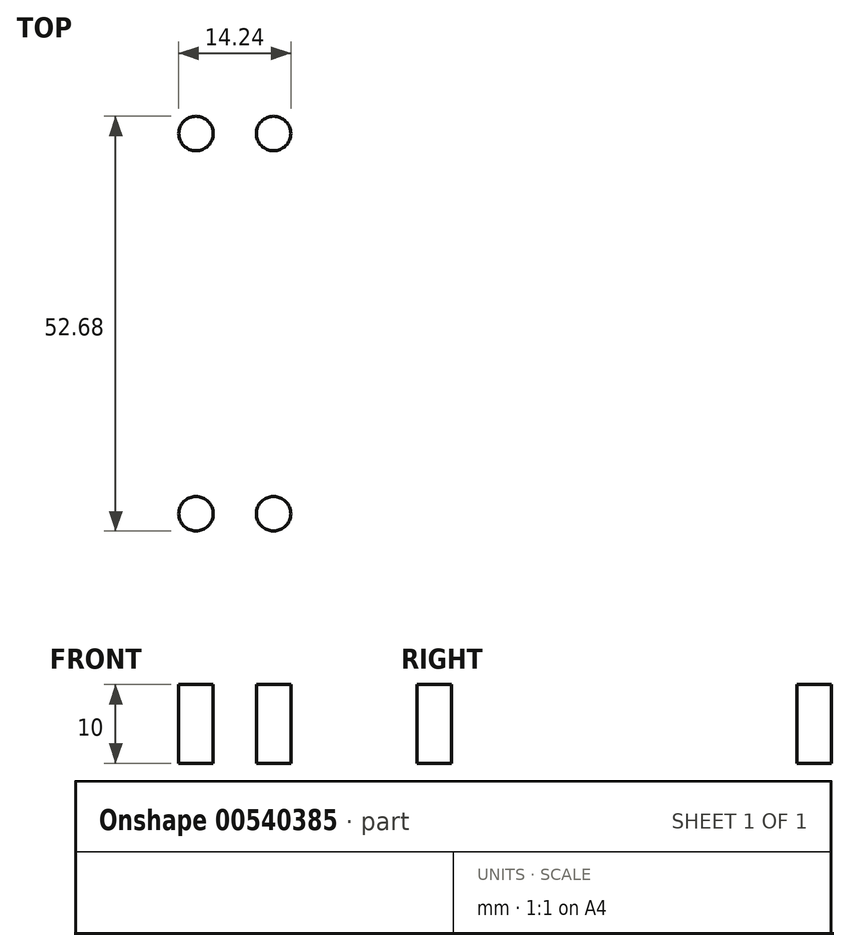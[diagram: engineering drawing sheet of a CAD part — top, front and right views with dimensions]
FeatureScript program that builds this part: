
annotation { "Feature Type Name" : "Feature", "Feature Type Description" : "" }
export const myFeature = defineFeature(function(context is Context, id is Id, definition is map)
    precondition{}
    {
        {
            var Q0;
            Q0=qCreatedBy(makeId("Top.planeOp"),FACE);
            var sketch = newSketch(context, id + "F0", { "sketchPlane" : qUnion([Q0])});
            skLineSegment(sketch, "E0.bottom", {"start": v(-110, 75) * mm, "end": v(110, 75) * mm});
            skLineSegment(sketch, "E0.top", {"start": v(-110, -75) * mm, "end": v(110, -75) * mm});
            skLineSegment(sketch, "E0.left", {"start": v(-110, 75) * mm, "end": v(-110, -75) * mm});
            skLineSegment(sketch, "E0.right", {"start": v(110, 75) * mm, "end": v(110, -75) * mm});
            skCircle(sketch, "E1", {"center": v(0, -5.5) * mm, "radius": 61.5 * mm});
            skLineSegment(sketch, "E2", {"start": v(0, 75) * mm, "end": v(0, -75) * mm, "construction": true});
            skSolve(sketch);
        }
        {
            var Q0;
            Q0=qCreatedBy(makeId("Top.planeOp"),FACE);
            var sketch = newSketch(context, id + "F1", { "sketchPlane" : qUnion([Q0])});
            skLineSegment(sketch, "E3.bottom", {"start": v(-90.22, 7.97) * mm, "end": v(-80.38, 7.97) * mm, "construction": true});
            skLineSegment(sketch, "E3.top", {"start": v(-90.22, -40.33) * mm, "end": v(-80.38, -40.33) * mm, "construction": true});
            skLineSegment(sketch, "E3.left", {"start": v(-90.22, 7.97) * mm, "end": v(-90.23, -40.33) * mm, "construction": true});
            skLineSegment(sketch, "E3.right", {"start": v(-80.38, 7.97) * mm, "end": v(-80.38, -40.33) * mm, "construction": true});
            skCircle(sketch, "E4", {"center": v(-90.22, 7.97) * mm, "radius": 2.19 * mm});
            skCircle(sketch, "E5", {"center": v(-80.38, 7.97) * mm, "radius": 2.19 * mm});
            skCircle(sketch, "E6", {"center": v(-80.38, -40.33) * mm, "radius": 2.19 * mm});
            skCircle(sketch, "E7", {"center": v(-90.22, -40.33) * mm, "radius": 2.19 * mm});
            skLineSegment(sketch, "E8.bottom", {"start": v(-95.3, 4.32) * mm, "end": v(-75.3, 4.32) * mm});
            skLineSegment(sketch, "E8.top", {"start": v(-95.3, -36.68) * mm, "end": v(-75.3, -36.68) * mm});
            skLineSegment(sketch, "E8.left", {"start": v(-95.3, 4.32) * mm, "end": v(-95.3, -36.68) * mm});
            skLineSegment(sketch, "E8.right", {"start": v(-75.3, 4.32) * mm, "end": v(-75.3, -36.68) * mm});
            skPoint(sketch, "E9", {"position": v(-80.38, -16.18) * mm});
            skPoint(sketch, "E10", {"position": v(-75.3, -16.18) * mm});
            skPoint(sketch, "E11", {"position": v(-85.3, 4.32) * mm});
            skPoint(sketch, "E12", {"position": v(-85.3, 7.97) * mm});
            skCircle(sketch, "E13", {"center": v(-85.3, -5.5) * mm, "radius": 3.7 * mm, "construction": true});
            skCircle(sketch, "E14.0", {"center": v(0, -5.5) * mm, "radius": 61.5 * mm});
            skCircle(sketch, "E15.MirrorC", {"center": v(80.38, -40.33) * mm, "radius": 2.19 * mm});
            skCircle(sketch, "E16.MirrorC", {"center": v(80.38, 7.97) * mm, "radius": 2.19 * mm});
            skCircle(sketch, "E17.MirrorC", {"center": v(90.22, 7.97) * mm, "radius": 2.19 * mm});
            skCircle(sketch, "E18.MirrorC", {"center": v(90.22, -40.33) * mm, "radius": 2.19 * mm});
            skLineSegment(sketch, "E19.MirrorCS", {"start": v(95.3, 4.32) * mm, "end": v(75.3, 4.32) * mm});
            skLineSegment(sketch, "E20.MirrorCS", {"start": v(90.22, 7.97) * mm, "end": v(80.38, 7.97) * mm, "construction": true});
            skPoint(sketch, "E21.MirrorP", {"position": v(85.3, 7.97) * mm});
            skPoint(sketch, "E22.MirrorP", {"position": v(75.3, -16.18) * mm});
            skLineSegment(sketch, "E23.MirrorCS", {"start": v(95.3, -36.68) * mm, "end": v(75.3, -36.68) * mm});
            skLineSegment(sketch, "E24.MirrorCS", {"start": v(80.38, 7.97) * mm, "end": v(80.38, -40.33) * mm, "construction": true});
            skLineSegment(sketch, "E25.MirrorCS", {"start": v(95.3, 4.32) * mm, "end": v(95.3, -36.68) * mm});
            skPoint(sketch, "E26.MirrorP", {"position": v(85.3, 4.32) * mm});
            skLineSegment(sketch, "E27.MirrorCS", {"start": v(75.3, 4.32) * mm, "end": v(75.3, -36.68) * mm});
            skPoint(sketch, "E28.MirrorP", {"position": v(80.38, -16.18) * mm});
            skCircle(sketch, "E29.MirrorC", {"center": v(85.3, -5.5) * mm, "radius": 3.7 * mm, "construction": true});
            skLineSegment(sketch, "E30.MirrorCS", {"start": v(90.22, -40.33) * mm, "end": v(80.38, -40.33) * mm, "construction": true});
            skLineSegment(sketch, "E31.MirrorCS", {"start": v(90.23, 7.97) * mm, "end": v(90.23, -40.33) * mm, "construction": true});
            skLineSegment(sketch, "E32.0", {"start": v(-110, 75) * mm, "end": v(110, 75) * mm});
            skLineSegment(sketch, "E32.1", {"start": v(-110, 75) * mm, "end": v(-110, -75) * mm});
            skLineSegment(sketch, "E32.2", {"start": v(-110, -75) * mm, "end": v(110, -75) * mm});
            skLineSegment(sketch, "E32.3", {"start": v(110, 75) * mm, "end": v(110, -75) * mm});
            skLineSegment(sketch, "E33", {"start": v(0, -5.5) * mm, "end": v(-110, -5.5) * mm, "construction": true});
            skSolve(sketch);
        }
        {
            var Q0;
            Q0 = qSketchRegion(id + "F0", true);
            extrude(context, id + "F2", {"entities" : qUnion([Q0]), "oppositeDirection" : true, "depth" : 10 * mm, "offsetDistance" : 25 * mm});
        }
        {
            var Q0;
            Q0=makeQuery(id+"F1.imprint","IMPRINT",FACE,{"disambiguationData":[TD([[makeQuery(id+"F1.imprint","IMPRINT",EDGE,{"derivedFrom":sQuery(id+"F1.wireOp",EDGE,"E8.bottom")}),-1.0]])]});
            var Q1;
            Q1=makeQuery(id+"F1.imprint","IMPRINT",FACE,{"disambiguationData":[TD([[makeQuery(id+"F1.imprint","IMPRINT",EDGE,{"derivedFrom":sQuery(id+"F1.wireOp",EDGE,"E5")}),1.0]])]});
            var Q2;
            Q2=makeQuery(id+"F1.imprint","IMPRINT",FACE,{"disambiguationData":[TD([[makeQuery(id+"F1.imprint","IMPRINT",EDGE,{"derivedFrom":sQuery(id+"F1.wireOp",EDGE,"E4")}),1.0]])]});
            var Q3;
            Q3=makeQuery(id+"F1.imprint","IMPRINT",FACE,{"disambiguationData":[TD([[makeQuery(id+"F1.imprint","IMPRINT",EDGE,{"derivedFrom":sQuery(id+"F1.wireOp",EDGE,"E6")}),1.0]])]});
            var Q4;
            Q4=makeQuery(id+"F1.imprint","IMPRINT",FACE,{"disambiguationData":[TD([[makeQuery(id+"F1.imprint","IMPRINT",EDGE,{"derivedFrom":sQuery(id+"F1.wireOp",EDGE,"E7")}),1.0]])]});
            var Q5;
            Q5=makeQuery(id+"F1.imprint","IMPRINT",FACE,{"disambiguationData":[TD([[makeQuery(id+"F1.imprint","IMPRINT",EDGE,{"derivedFrom":sQuery(id+"F1.wireOp",EDGE,"E19.MirrorCS")}),1.0]])]});
            var Q6;
            Q6=makeQuery(id+"F1.imprint","IMPRINT",FACE,{"disambiguationData":[TD([[makeQuery(id+"F1.imprint","IMPRINT",EDGE,{"derivedFrom":sQuery(id+"F1.wireOp",EDGE,"E16.MirrorC")}),-1.0]])]});
            var Q7;
            Q7=makeQuery(id+"F1.imprint","IMPRINT",FACE,{"disambiguationData":[TD([[makeQuery(id+"F1.imprint","IMPRINT",EDGE,{"derivedFrom":sQuery(id+"F1.wireOp",EDGE,"E17.MirrorC")}),-1.0]])]});
            var Q8;
            Q8=makeQuery(id+"F1.imprint","IMPRINT",FACE,{"disambiguationData":[TD([[makeQuery(id+"F1.imprint","IMPRINT",EDGE,{"derivedFrom":sQuery(id+"F1.wireOp",EDGE,"E15.MirrorC")}),-1.0]])]});
            var Q9;
            Q9=makeQuery(id+"F1.imprint","IMPRINT",FACE,{"disambiguationData":[TD([[makeQuery(id+"F1.imprint","IMPRINT",EDGE,{"derivedFrom":sQuery(id+"F1.wireOp",EDGE,"E18.MirrorC")}),-1.0]])]});
            extrude(context, id + "F3", {"entities" : qUnion([Q0, Q1, Q2, Q3, Q4, Q5, Q6, Q7, Q8, Q9]), "operationType" : NewBodyOperationType.REMOVE, "endBound" : BoundingType.UP_TO_NEXT, "oppositeDirection" : true, "depth" : 25 * mm, "offsetDistance" : 25 * mm});
        }
    });
